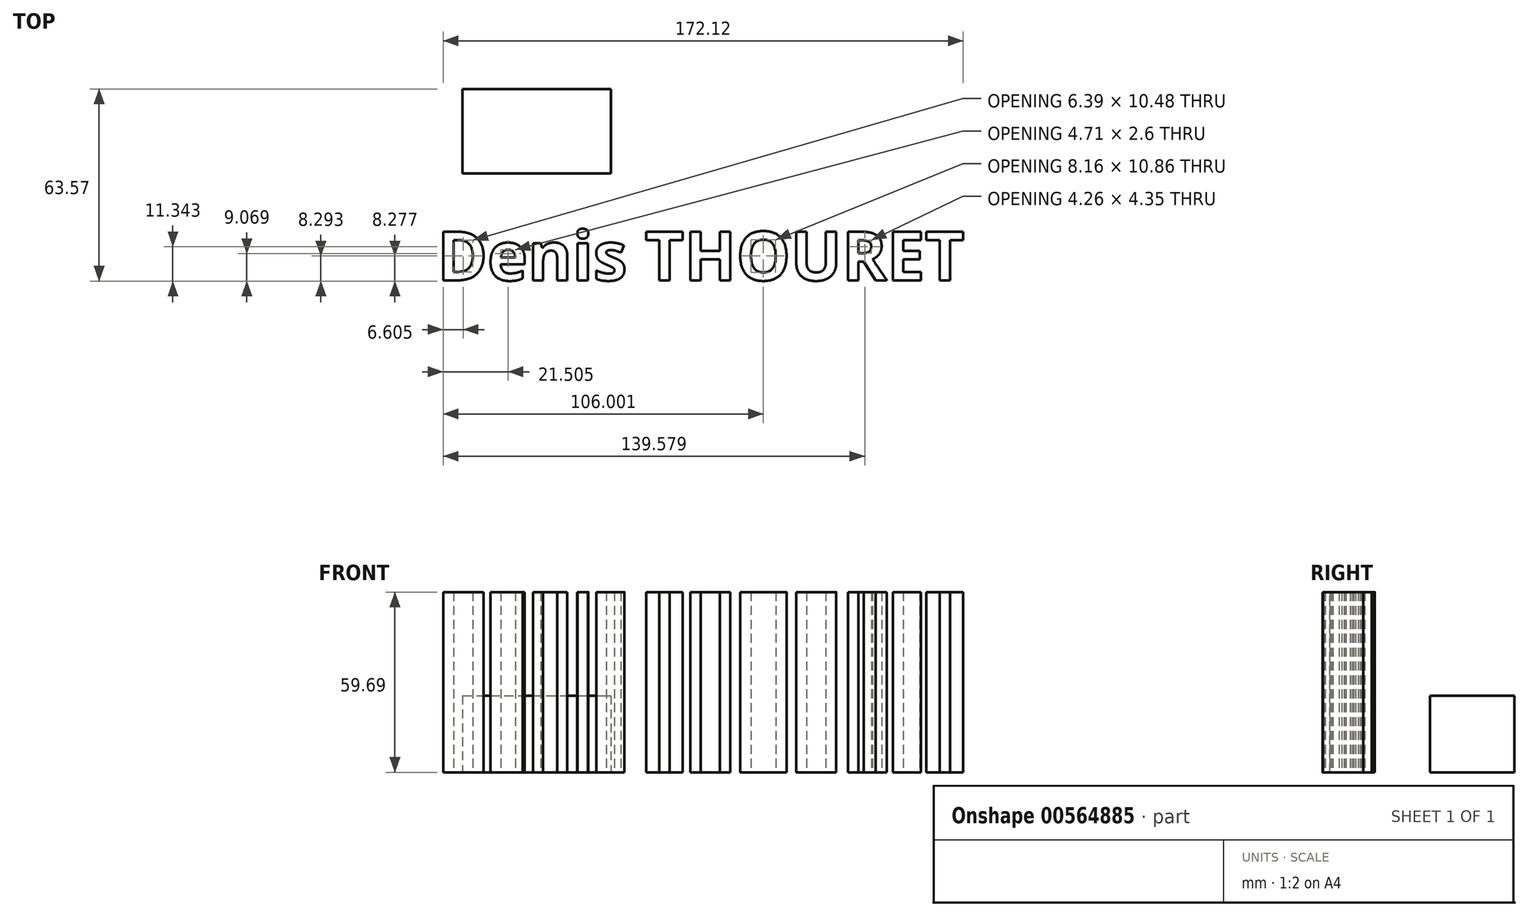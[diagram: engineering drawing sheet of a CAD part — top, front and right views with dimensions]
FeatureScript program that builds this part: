
annotation { "Feature Type Name" : "Feature", "Feature Type Description" : "" }
export const myFeature = defineFeature(function(context is Context, id is Id, definition is map)
    precondition{}
    {
        {
            var Q0;
            Q0=qCreatedBy(makeId("Top.planeOp"),FACE);
            var sketch = newSketch(context, id + "F0", { "sketchPlane" : qUnion([Q0])});
            skLineSegment(sketch, "E0.bottom", {"start": v(-29.53, 0) * mm, "end": v(19.57, 0) * mm});
            skLineSegment(sketch, "E0.top", {"start": v(-29.53, 27.95) * mm, "end": v(19.57, 27.95) * mm});
            skLineSegment(sketch, "E0.left", {"start": v(-29.53, 0) * mm, "end": v(-29.53, 27.95) * mm});
            skLineSegment(sketch, "E0.right", {"start": v(19.57, 0) * mm, "end": v(19.57, 27.95) * mm});
            skSolve(sketch);
        }
        {
            var Q0;
            Q0 = qSketchRegion(id + "F0", true);
            extrude(context, id + "F1", {"entities" : qUnion([Q0]), "depth" : 25.4 * mm, "offsetDistance" : 25.4 * mm});
        }
        {
            var Q0;
            Q0=qCreatedBy(makeId("Top.planeOp"),FACE);
            var sketch = newSketch(context, id + "F2", { "sketchPlane" : qUnion([Q0])});
            skCircle(sketch, "E1", {"center": v(-95.97, 0) * mm, "radius": 39.1 * mm});
            skSolve(sketch);
        }
        {
            var Q0;
            Q0=sQuery(id+"F2.wireOp",EDGE,"E1");
            extrude(context, id + "F3", {"bodyType" : ToolBodyType.SURFACE, "surfaceEntities" : qUnion([Q0]), "depth" : 40.9 * mm, "offsetDistance" : 25.4 * mm});
        }
        {
            var Q0;
            Q0=qCreatedBy(makeId("Top.planeOp"),FACE);
            var sketch = newSketch(context, id + "F4", { "sketchPlane" : qUnion([Q0])});
            skText(sketch, "E2", { "text": "Denis THOURET", "fontName": "OpenSans-Bold.ttf"});
            const initialGuessF4  = {"E2": [-0.038, -0.0354, 1, 0, 0.01623]};
            skSetInitialGuess(sketch, initialGuessF4);
            skSolve(sketch);
        }
        {
            var Q0;
            Q0 = qSketchRegion(id + "F4", true);
            extrude(context, id + "F5", {"entities" : qUnion([Q0]), "depth" : 59.69 * mm, "offsetDistance" : 25.4 * mm});
        }
    });
